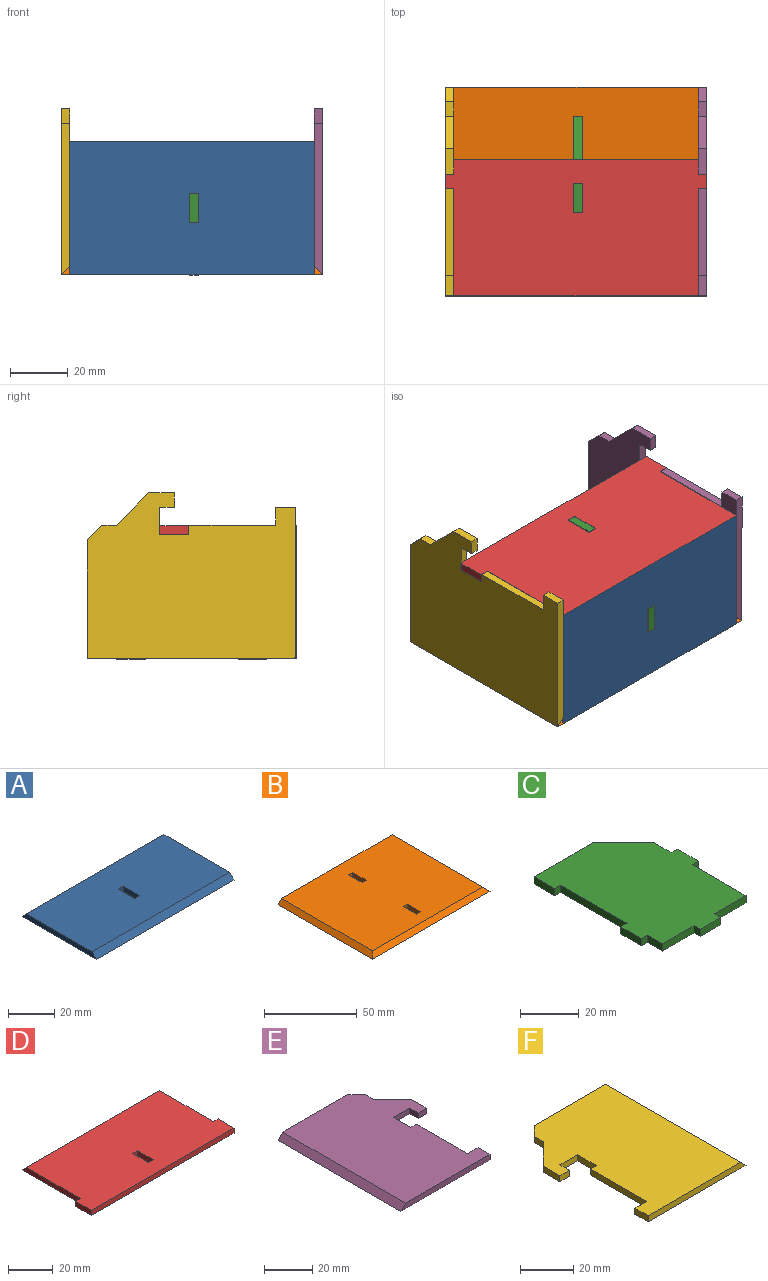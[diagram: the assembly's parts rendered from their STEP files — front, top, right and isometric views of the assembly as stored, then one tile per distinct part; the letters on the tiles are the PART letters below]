
ASSEMBLY  parts=6 mates=5
PART A: 10 faces, bbox 84.4x45.8x2.8 mm
  f0: plane 84.4x40.2mm, normal (0,0,1), area 3361.6mm2, adj f2,f3,f4,f5,f6,f7,f8,f9
  f1: plane 84.4x45.8mm, normal (0,0,-1), area 3834.2mm2, adj f2,f3,f4,f5,f6,f7,f8,f9
  f2: plane 45.8x2.8mm, normal (1,0,0), area 120.4mm2, adj f0,f1,f4,f5
  f3: plane 45.8x2.8mm, normal (-1,0,0), area 120.4mm2, adj f0,f1,f4,f5
  f4: plane 84.4x2.8mm, normal (0,-0.71,0.71), area 334.2mm2, adj f0,f1,f2,f3
  f5: plane 84.4x2.8mm, normal (0,0.71,0.71), area 334.2mm2, adj f0,f1,f2,f3
  f6: plane 3.1x2.8mm, normal (0,-1,0), area 8.7mm2, adj f0,f1,f7,f9
  f7: plane 10.1x2.8mm, normal (1,0,0), area 28.3mm2, adj f0,f1,f6,f8
  f8: plane 3.1x2.8mm, normal (0,1,0), area 8.7mm2, adj f0,f1,f7,f9
  f9: plane 10.1x2.8mm, normal (-1,0,0), area 28.3mm2, adj f0,f1,f6,f8
PART B: 14 faces, bbox 90x72x2.8 mm
  f0: plane 84.4x69.2mm, normal (0,0,1), area 5777.9mm2, adj f2,f3,f4,f5,f6,f7,f8,f9
  f1: plane 90x72mm, normal (0,0,-1), area 6417.4mm2, adj f2,f3,f4,f5,f6,f7,f8,f9
  f2: plane 90x2.8mm, normal (0,1,0), area 244.2mm2, adj f0,f1,f3,f4
  f3: plane 72x2.8mm, normal (0.71,0,0.71), area 279.6mm2, adj f0,f1,f2,f5
  f4: plane 72x2.8mm, normal (-0.71,0,0.71), area 279.6mm2, adj f0,f1,f2,f5
  f5: plane 90x2.8mm, normal (0,-0.71,0.71), area 345.3mm2, adj f0,f1,f3,f4
  f6: plane 3.1x2.8mm, normal (0,-1,0), area 8.7mm2, adj f0,f1,f7,f9
  f7: plane 10.1x2.8mm, normal (1,0,0), area 28.3mm2, adj f0,f1,f6,f8
  f8: plane 3.1x2.8mm, normal (0,1,0), area 8.7mm2, adj f0,f1,f7,f9
  f9: plane 10.1x2.8mm, normal (-1,0,0), area 28.3mm2, adj f0,f1,f6,f8
  f10: plane 3.1x2.8mm, normal (0,-1,0), area 8.7mm2, adj f0,f1,f11,f13
  f11: plane 10.1x2.8mm, normal (1,0,0), area 28.3mm2, adj f0,f1,f10,f12
  f12: plane 3.1x2.8mm, normal (0,1,0), area 8.7mm2, adj f0,f1,f11,f13
  f13: plane 10.1x2.8mm, normal (-1,0,0), area 28.3mm2, adj f0,f1,f10,f12
PART C: 21 faces, bbox 46.2x62.2x3 mm
  f0: plane 28.2x3mm, normal (0,1,0), area 84.6mm2, adj f1,f18,f19,f20
  f1: plane 10x3mm, normal (-1,0,0), area 30mm2, adj f0,f2,f18,f19
  f2: plane 3x3mm, normal (0,-1,0), area 9mm2, adj f1,f3,f18,f19
  f3: plane 31.9x3mm, normal (-1,0,0), area 95.7mm2, adj f2,f4,f18,f19
  f4: plane 3x3mm, normal (0,1,0), area 9mm2, adj f3,f5,f18,f19
  f5: plane 10x3mm, normal (-1,0,0), area 30mm2, adj f4,f6,f18,f19
  f6: plane 3x3mm, normal (0,-1,0), area 9mm2, adj f5,f7,f18,f19
  f7: plane 7.25x3mm, normal (-1,0,0), area 21.8mm2, adj f6,f8,f18,f19
  f8: plane 15.1x3mm, normal (0,-1,0), area 45.3mm2, adj f7,f9,f18,f19
  f9: plane 3x3mm, normal (-1,0,0), area 9mm2, adj f8,f10,f18,f19
  f10: plane 10x3mm, normal (0,-1,0), area 30mm2, adj f9,f11,f18,f19
  f11: plane 3x3mm, normal (1,0,0), area 9mm2, adj f10,f12,f18,f19
  f12: plane 15.1x3mm, normal (0,-1,0), area 45.3mm2, adj f11,f13,f18,f19
  f13: plane 26.05x3mm, normal (1,0,0), area 78.2mm2, adj f12,f14,f18,f19
  f14: plane 3x3mm, normal (0,-1,0), area 9mm2, adj f13,f15,f18,f19
  f15: plane 10x3mm, normal (1,0,0), area 30mm2, adj f14,f16,f18,f19
  f16: plane 3x3mm, normal (0,1,0), area 9mm2, adj f15,f17,f18,f19
  f17: plane 8.1x3mm, normal (1,0,0), area 24.3mm2, adj f16,f18,f19,f20
  f18: plane 62.15x46.2mm, normal (0,0,1), area 2385.3mm2, adj f0,f1,f2,f3,f4,f5,f6,f7
  f19: plane 62.15x46.2mm, normal (0,0,-1), area 2385.3mm2, adj f0,f1,f2,f3,f4,f5,f6,f7
  f20: plane 15x15mm, normal (0.71,0.71,0), area 63.6mm2, adj f0,f17,f18,f19
PART D: 14 faces, bbox 90.4x47x2.8 mm
  f0: plane 90.4x44.2mm, normal (0,0,1), area 3759.2mm2, adj f2,f3,f4,f5,f6,f7,f8,f9
  f1: plane 90.4x47mm, normal (0,0,-1), area 3995.5mm2, adj f2,f3,f4,f5,f6,f7,f8,f9
  f2: plane 37x2.8mm, normal (-1,0,0), area 99.7mm2, adj f0,f1,f5,f6
  f3: plane 90.4x2.8mm, normal (0,-1,0), area 253.1mm2, adj f0,f1,f7,f9
  f4: plane 37x2.8mm, normal (1,0,0), area 99.7mm2, adj f0,f1,f5,f8
  f5: plane 84.4x2.8mm, normal (0,0.71,0.71), area 334.2mm2, adj f0,f1,f2,f4
  f6: plane 3x2.8mm, normal (0,1,0), area 8.4mm2, adj f0,f1,f2,f7
  f7: plane 10x2.8mm, normal (-1,0,0), area 28mm2, adj f0,f1,f3,f6
  f8: plane 3x2.8mm, normal (0,1,0), area 8.4mm2, adj f0,f1,f4,f9
  f9: plane 10x2.8mm, normal (1,0,0), area 28mm2, adj f0,f1,f3,f8
  f10: plane 3.1x2.8mm, normal (0,-1,0), area 8.7mm2, adj f0,f1,f11,f13
  f11: plane 10.1x2.8mm, normal (1,0,0), area 28.3mm2, adj f0,f1,f10,f12
  f12: plane 3.1x2.8mm, normal (0,1,0), area 8.7mm2, adj f0,f1,f11,f13
  f13: plane 10.1x2.8mm, normal (-1,0,0), area 28.3mm2, adj f0,f1,f10,f12
PART E: 17 faces, bbox 57.2x72x2.8 mm
  f0: plane 41x2.8mm, normal (0,1,0), area 110.9mm2, adj f13,f14,f15,f16
  f1: plane 52.2x2.8mm, normal (0,-1,0), area 142.2mm2, adj f2,f13,f14,f15
  f2: plane 7x2.8mm, normal (1,0,0), area 19.6mm2, adj f1,f3,f13,f14
  f3: plane 6.2x2.8mm, normal (0,1,0), area 17.4mm2, adj f2,f4,f13,f14
  f4: plane 30x2.8mm, normal (1,0,0), area 84mm2, adj f3,f5,f13,f14
  f5: plane 3.2x2.8mm, normal (0,1,0), area 9mm2, adj f4,f6,f13,f14
  f6: plane 10x2.8mm, normal (1,0,0), area 28mm2, adj f5,f7,f13,f14
  f7: plane 9.4x2.8mm, normal (0,-1,0), area 26.3mm2, adj f6,f8,f13,f14
  f8: plane 5x2.8mm, normal (-1,0,0), area 14mm2, adj f7,f9,f13,f14
  f9: plane 5x2.8mm, normal (0,-1,0), area 14mm2, adj f8,f10,f13,f14
  f10: plane 8.8x2.8mm, normal (1,0,0), area 24.6mm2, adj f9,f11,f13,f14
  f11: plane 11.2x11.2mm, normal (0.71,0.71,0), area 44.3mm2, adj f10,f12,f13,f14
  f12: plane 5x2.8mm, normal (1,0,0), area 14mm2, adj f11,f13,f14,f16
  f13: plane 72x54.4mm, normal (0,0,1), area 3239.6mm2, adj f0,f1,f2,f3,f4,f5,f6,f7
  f14: plane 72x57.2mm, normal (0,0,-1), area 3441.2mm2, adj f0,f1,f2,f3,f4,f5,f6,f7
  f15: plane 72x2.8mm, normal (-0.71,0,0.71), area 285.1mm2, adj f0,f1,f13,f14
  f16: plane 5x5mm, normal (0.71,0.71,0), area 19.8mm2, adj f0,f12,f13,f14
PART F: 17 faces, bbox 57.2x72x2.8 mm
  f0: plane 52.2x2.8mm, normal (0,-1,0), area 142.2mm2, adj f12,f13,f14,f15
  f1: plane 41x2.8mm, normal (0,1,0), area 110.9mm2, adj f13,f14,f15,f16
  f2: plane 5x2.8mm, normal (-1,0,0), area 14mm2, adj f3,f13,f14,f16
  f3: plane 11.2x11.2mm, normal (-0.71,0.71,0), area 44.3mm2, adj f2,f4,f13,f14
  f4: plane 8.8x2.8mm, normal (-1,0,0), area 24.6mm2, adj f3,f5,f13,f14
  f5: plane 5x2.8mm, normal (0,-1,0), area 14mm2, adj f4,f6,f13,f14
  f6: plane 5x2.8mm, normal (1,0,0), area 14mm2, adj f5,f7,f13,f14
  f7: plane 9.4x2.8mm, normal (0,-1,0), area 26.3mm2, adj f6,f8,f13,f14
  f8: plane 10x2.8mm, normal (-1,0,0), area 28mm2, adj f7,f9,f13,f14
  f9: plane 3.2x2.8mm, normal (0,1,0), area 9mm2, adj f8,f10,f13,f14
  f10: plane 30x2.8mm, normal (-1,0,0), area 84mm2, adj f9,f11,f13,f14
  f11: plane 6.2x2.8mm, normal (0,1,0), area 17.4mm2, adj f10,f12,f13,f14
  f12: plane 7x2.8mm, normal (-1,0,0), area 19.6mm2, adj f0,f11,f13,f14
  f13: plane 72x54.4mm, normal (0,0,1), area 3239.6mm2, adj f0,f1,f2,f3,f4,f5,f6,f7
  f14: plane 72x57.2mm, normal (0,0,-1), area 3441.2mm2, adj f0,f1,f2,f3,f4,f5,f6,f7
  f15: plane 72x2.8mm, normal (0.71,0,0.71), area 285.1mm2, adj f0,f1,f13,f14
  f16: plane 5x5mm, normal (-0.71,0.71,0), area 19.8mm2, adj f1,f2,f13,f14
PLACE A rot(axis=(-1,0,0),90deg) t=(0,-36.01,-36.01)mm
PLACE B at identity fixed
PLACE C rot(axis=(0,-1,0),90deg) t=(2.2,94.79,-79.35)mm
PLACE D rot(axis=(-1,0,0),180deg) t=(0,-117.81,45.79)mm
PLACE E rot(axis=(0,-1,0),90deg) t=(45.01,0,-45.01)mm
PLACE F rot(axis=(0,1,0),90deg) t=(-45.01,0,-45.01)mm
MATE fastened B.f5 <-> A.f5  axis (0,-0.71,0.71) through (0,-34.61,1.39)mm
MATE fastened C.f3 <-> B.f0  axis (0,0,-1) through (2.2,15.9,2.8)mm
MATE fastened A.f4 <-> D.f5  axis (0,0.71,0.71) through (0,-34.61,44.39)mm
MATE fastened B.f4 <-> F.f15  axis (-0.71,0,0.71) through (-43.61,0.7,1.39)mm
MATE fastened B.f3 <-> E.f15  axis (0.71,0,0.71) through (43.61,0.7,1.39)mm
